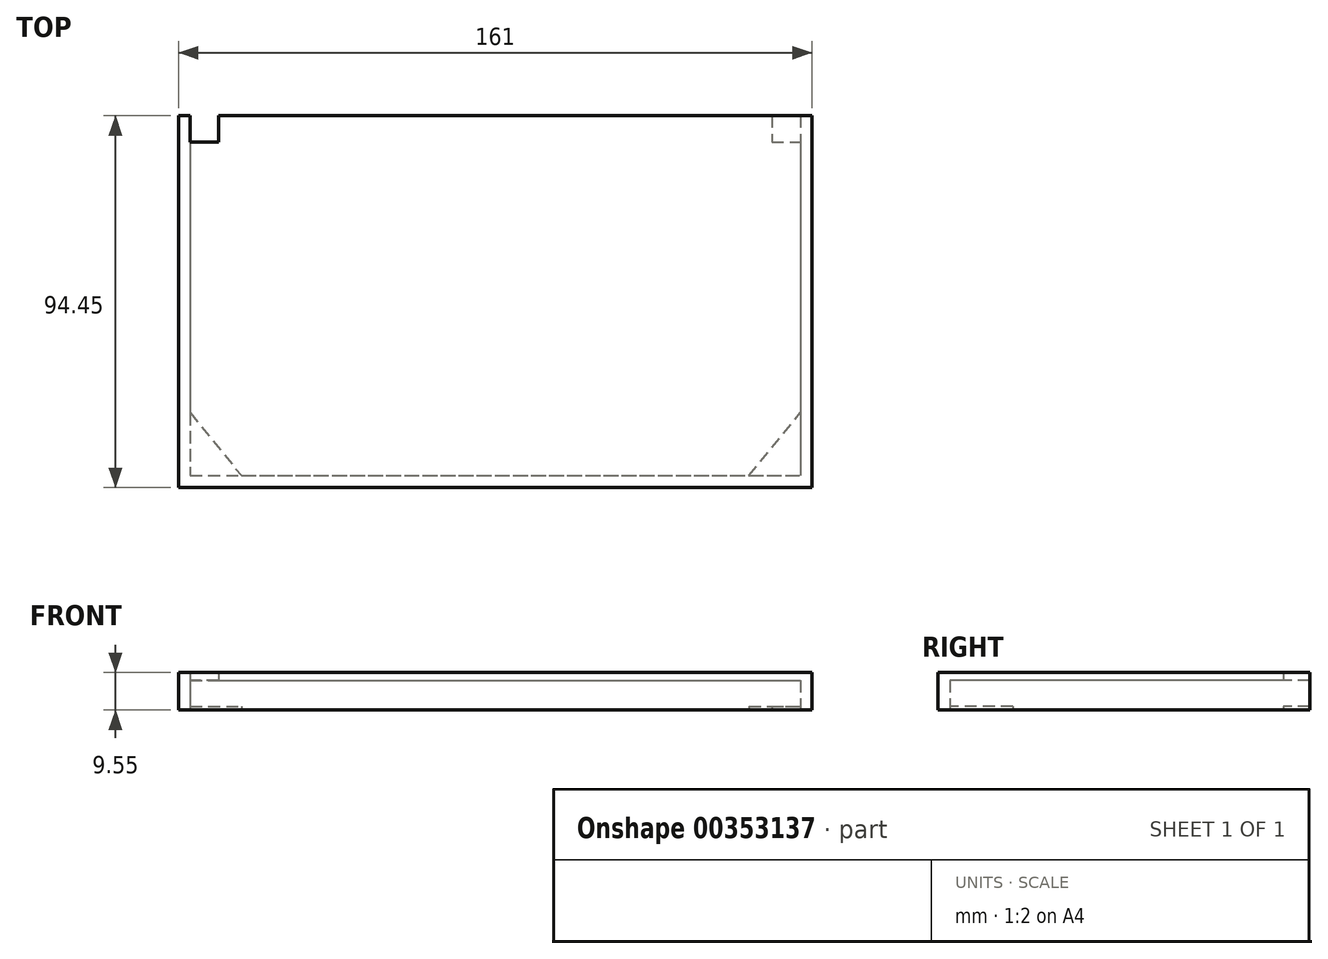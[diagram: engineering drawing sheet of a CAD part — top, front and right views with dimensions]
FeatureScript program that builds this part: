
annotation { "Feature Type Name" : "Feature", "Feature Type Description" : "" }
export const myFeature = defineFeature(function(context is Context, id is Id, definition is map)
    precondition{}
    {
        {
            var Q0;
            Q0=qCreatedBy(makeId("Top.planeOp"),FACE);
            var sketch = newSketch(context, id + "F0", { "sketchPlane" : qUnion([Q0])});
            skLineSegment(sketch, "E0.bottom", {"start": v(-80.6, 83.37) * mm, "end": v(74.4, 83.37) * mm});
            skLineSegment(sketch, "E0.top", {"start": v(-80.6, -8.08) * mm, "end": v(74.4, -8.08) * mm});
            skLineSegment(sketch, "E0.left", {"start": v(-80.6, 83.37) * mm, "end": v(-80.6, -8.08) * mm});
            skLineSegment(sketch, "E0.right", {"start": v(74.4, 83.37) * mm, "end": v(74.4, -8.08) * mm});
            skLineSegment(sketch, "E1.bottom", {"start": v(-83.6, -11.08) * mm, "end": v(77.4, -11.08) * mm});
            skLineSegment(sketch, "E1.top", {"start": v(-83.6, 83.37) * mm, "end": v(77.4, 83.37) * mm});
            skLineSegment(sketch, "E1.left", {"start": v(-83.6, -11.08) * mm, "end": v(-83.6, 83.37) * mm});
            skLineSegment(sketch, "E1.right", {"start": v(77.4, -11.08) * mm, "end": v(77.4, 83.37) * mm});
            skLineSegment(sketch, "E2", {"start": v(-80.6, 7.92) * mm, "end": v(-67.6, -8.08) * mm});
            skLineSegment(sketch, "E3", {"start": v(61.4, -8.08) * mm, "end": v(74.4, 7.92) * mm});
            skLineSegment(sketch, "E4", {"start": v(-80.6, 83.37) * mm, "end": v(-73.39, 83.37) * mm});
            skLineSegment(sketch, "E5", {"start": v(-73.39, 83.37) * mm, "end": v(-73.39, 76.7) * mm});
            skLineSegment(sketch, "E6", {"start": v(-73.39, 76.7) * mm, "end": v(-80.6, 76.7) * mm});
            skLineSegment(sketch, "E7", {"start": v(77.4, 83.37) * mm, "end": v(67.18, 83.37) * mm});
            skLineSegment(sketch, "E8", {"start": v(67.18, 83.37) * mm, "end": v(67.18, 76.7) * mm});
            skLineSegment(sketch, "E9", {"start": v(67.18, 76.7) * mm, "end": v(74.4, 76.7) * mm});
            skSolve(sketch);
        }
        {
            var Q0;
            Q0=makeQuery(id+"F0.imprint","IMPRINT",FACE,{"disambiguationData":[TD([[makeQuery(id+"F0.imprint","IMPRINT",EDGE,{"derivedFrom":sQuery(id+"F0.wireOp",EDGE,"E1.bottom")}),1.0]])]});
            var Q1;
            {var subQ3=sQuery(id+"F0.wireOp",EDGE,"E2");Q1=makeQuery(id+"F0.imprint","IMPRINT",FACE,{"disambiguationData":[TD([[makeQuery(id+"F0.imprint","IMPRINT",EDGE,{"derivedFrom":subQ3}),-1.0]])]});}
            var Q2;
            {var subQ3=sQuery(id+"F0.wireOp",EDGE,"E3");Q2=makeQuery(id+"F0.imprint","IMPRINT",FACE,{"disambiguationData":[TD([[makeQuery(id+"F0.imprint","IMPRINT",EDGE,{"derivedFrom":subQ3}),-1.0]])]});}
            var Q3;
            {var subQ6=sQuery(id+"F0.wireOp",EDGE,"E2");Q3=makeQuery(id+"F0.imprint","IMPRINT",FACE,{"disambiguationData":[TD([[makeQuery(id+"F0.imprint","IMPRINT",EDGE,{"derivedFrom":subQ6}),1.0]])]});}
            var Q4;
            {var subQ4=sQuery(id+"F0.wireOp",EDGE,"E8");Q4=makeQuery(id+"F0.imprint","IMPRINT",FACE,{"disambiguationData":[TD([[makeQuery(id+"F0.imprint","IMPRINT",EDGE,{"derivedFrom":subQ4}),1.0]])]});}
            var Q5;
            {var subQ0=sQuery(id+"F0.wireOp",EDGE,"E4");Q5=makeQuery(id+"F0.imprint","IMPRINT",FACE,{"disambiguationData":[TD([[makeQuery(id+"F0.imprint","IMPRINT",EDGE,{"derivedFrom":subQ0}),-1.0]])]});}
            extrude(context, id + "F1", {"entities" : qUnion([Q0, Q1, Q2, Q3, Q4, Q5]), "depth" : 9.55 * mm});
        }
        {
            var Q0;
            {var subQ4=sQuery(id+"F0.wireOp",EDGE,"E2");Q0=makeQuery(id+"F0.imprint","IMPRINT",FACE,{"disambiguationData":[TD([[makeQuery(id+"F0.imprint","IMPRINT",EDGE,{"derivedFrom":subQ4}),1.0]])]});}
            var Q1;
            {var subQ3=sQuery(id+"F0.wireOp",EDGE,"E2");Q1=makeQuery(id+"F0.imprint","IMPRINT",FACE,{"disambiguationData":[TD([[makeQuery(id+"F0.imprint","IMPRINT",EDGE,{"derivedFrom":subQ3}),-1.0]])]});}
            var Q2;
            {var subQ3=sQuery(id+"F0.wireOp",EDGE,"E3");Q2=makeQuery(id+"F0.imprint","IMPRINT",FACE,{"disambiguationData":[TD([[makeQuery(id+"F0.imprint","IMPRINT",EDGE,{"derivedFrom":subQ3}),-1.0]])]});}
            var Q3;
            {var subQ4=sQuery(id+"F0.wireOp",EDGE,"E8");Q3=makeQuery(id+"F0.imprint","IMPRINT",FACE,{"disambiguationData":[TD([[makeQuery(id+"F0.imprint","IMPRINT",EDGE,{"derivedFrom":subQ4}),1.0]])]});}
            var Q4;
            {var subQ0=sQuery(id+"F0.wireOp",EDGE,"E4");Q4=makeQuery(id+"F0.imprint","IMPRINT",FACE,{"disambiguationData":[TD([[makeQuery(id+"F0.imprint","IMPRINT",EDGE,{"derivedFrom":subQ0}),-1.0]])]});}
            extrude(context, id + "F2", {"entities" : qUnion([Q0, Q1, Q2, Q3, Q4]), "operationType" : NewBodyOperationType.REMOVE, "depth" : 7.55 * mm});
        }
        {
            var Q0;
            {var subQ3=sQuery(id+"F0.wireOp",EDGE,"E2");Q0=makeQuery(id+"F0.imprint","IMPRINT",FACE,{"disambiguationData":[TD([[makeQuery(id+"F0.imprint","IMPRINT",EDGE,{"derivedFrom":subQ3}),-1.0]])]});}
            var Q1;
            {var subQ3=sQuery(id+"F0.wireOp",EDGE,"E3");Q1=makeQuery(id+"F0.imprint","IMPRINT",FACE,{"disambiguationData":[TD([[makeQuery(id+"F0.imprint","IMPRINT",EDGE,{"derivedFrom":subQ3}),-1.0]])]});}
            var Q2;
            {var subQ4=sQuery(id+"F0.wireOp",EDGE,"E8");Q2=makeQuery(id+"F0.imprint","IMPRINT",FACE,{"disambiguationData":[TD([[makeQuery(id+"F0.imprint","IMPRINT",EDGE,{"derivedFrom":subQ4}),1.0]])]});}
            var Q3;
            {var subQ0=sQuery(id+"F0.wireOp",EDGE,"E4");Q3=makeQuery(id+"F0.imprint","IMPRINT",FACE,{"disambiguationData":[TD([[makeQuery(id+"F0.imprint","IMPRINT",EDGE,{"derivedFrom":subQ0}),-1.0]])]});}
            extrude(context, id + "F3", {"entities" : qUnion([Q0, Q1, Q2, Q3]), "operationType" : NewBodyOperationType.ADD, "depth" : 1 * mm});
        }
    });
